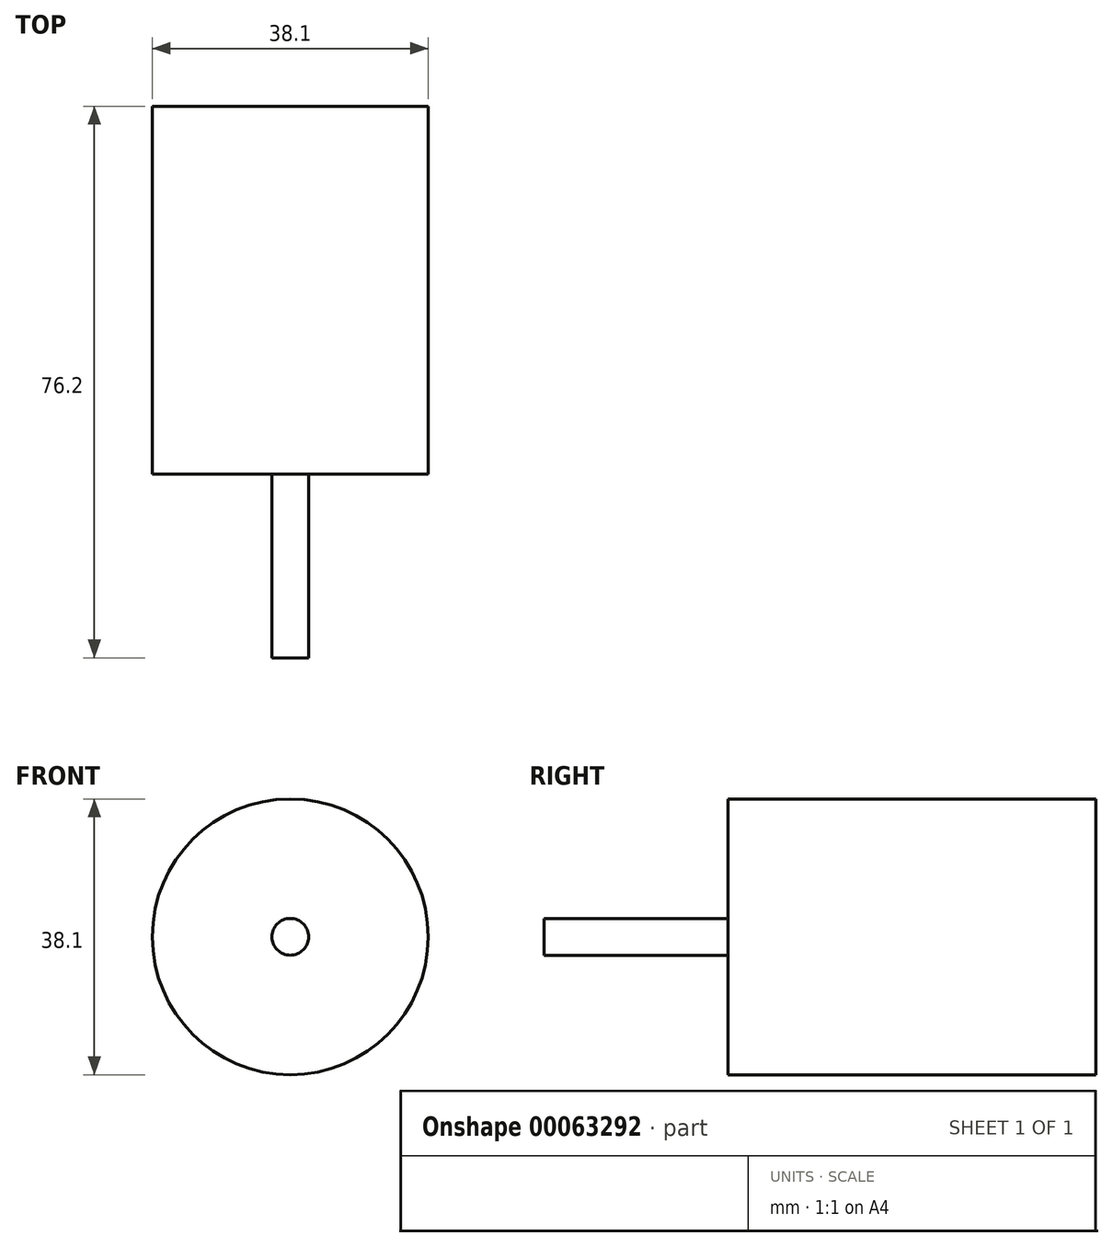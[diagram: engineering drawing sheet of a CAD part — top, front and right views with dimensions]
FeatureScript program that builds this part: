
annotation { "Feature Type Name" : "Feature", "Feature Type Description" : "" }
export const myFeature = defineFeature(function(context is Context, id is Id, definition is map)
    precondition{}
    {
        {
            var Q0;
            Q0=qCreatedBy(makeId("Front.planeOp"),FACE);
            var sketch = newSketch(context, id + "F0", { "sketchPlane" : qUnion([Q0])});
            skCircle(sketch, "E0", {"center": v(0, 0) * mm, "radius": 19.05 * mm});
            skSolve(sketch);
        }
        {
            var Q0;
            Q0 = qSketchRegion(id + "F0", true);
            extrude(context, id + "F1", {"entities" : qUnion([Q0]), "depth" : 50.8 * mm, "symmetric" : true});
        }
        {
            var Q0;
            Q0=makeQuery(id+"F1.opExtrude","CAP_FACE",FACE,{"disambiguationData":[OSD([sQuery(id+"F0.wireOp",EDGE,"E0")])],"isStart":false});
            var sketch = newSketch(context, id + "F2", { "sketchPlane" : qUnion([Q0])});
            skCircle(sketch, "E1", {"center": v(0, 0) * mm, "radius": 2.54 * mm});
            skSolve(sketch);
        }
        {
            var Q0;
            Q0 = qSketchRegion(id + "F2", true);
            extrude(context, id + "F3", {"entities" : qUnion([Q0]), "operationType" : NewBodyOperationType.ADD, "depth" : 25.4 * mm});
        }
    });
